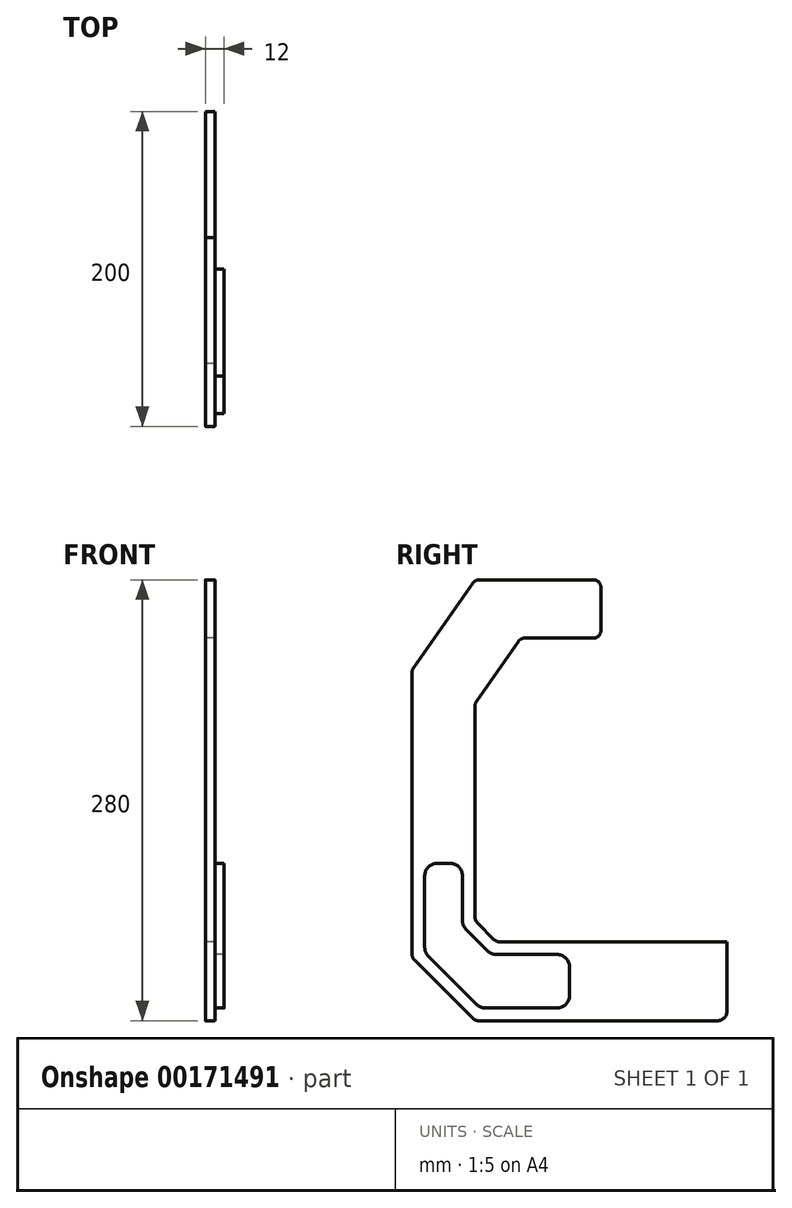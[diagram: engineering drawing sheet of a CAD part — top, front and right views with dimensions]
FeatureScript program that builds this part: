
annotation { "Feature Type Name" : "Feature", "Feature Type Description" : "" }
export const myFeature = defineFeature(function(context is Context, id is Id, definition is map)
    precondition{}
    {
        {
            var Q0;
            Q0=qCreatedBy(makeId("Right.planeOp"),FACE);
            var sketch = newSketch(context, id + "F0", { "sketchPlane" : qUnion([Q0])});
            skLineSegment(sketch, "E0", {"start": v(0, 0) * mm, "end": v(-160, 0) * mm});
            skLineSegment(sketch, "E1", {"start": v(-160, 0) * mm, "end": v(-200, 40) * mm});
            skLineSegment(sketch, "E2", {"start": v(-200, 40) * mm, "end": v(-200, 222.87) * mm});
            skLineSegment(sketch, "E3", {"start": v(-200, 222.87) * mm, "end": v(-160, 280) * mm});
            skLineSegment(sketch, "E4", {"start": v(-160, 280) * mm, "end": v(-80, 280) * mm});
            skLineSegment(sketch, "E5", {"start": v(-80, 280) * mm, "end": v(-80, 243) * mm});
            skLineSegment(sketch, "E6", {"start": v(-80, 243) * mm, "end": v(-130.97, 243) * mm});
            skLineSegment(sketch, "E7", {"start": v(-130.97, 243) * mm, "end": v(-160, 201.54) * mm});
            skLineSegment(sketch, "E8", {"start": v(-160, 201.54) * mm, "end": v(-160, 63.64) * mm});
            skLineSegment(sketch, "E9", {"start": v(-160, 63.64) * mm, "end": v(-146.36, 50) * mm});
            skLineSegment(sketch, "E10", {"start": v(-146.36, 50) * mm, "end": v(0, 50) * mm});
            skLineSegment(sketch, "E11", {"start": v(0, 50) * mm, "end": v(0, 0) * mm});
            skSolve(sketch);
        }
        {
            var Q0;
            Q0=makeQuery(id+"F0.imprint","IMPRINT",FACE,{"disambiguationData":[TD([[makeQuery(id+"F0.imprint","IMPRINT",EDGE,{"derivedFrom":sQuery(id+"F0.wireOp",EDGE,"E0")}),-1.0]])]});
            extrude(context, id + "F1", {"entities" : qUnion([Q0]), "depth" : 6 * mm});
        }
        {
            var Q0;
            Q0=makeQuery(id+"F1.opExtrude","SWEPT_EDGE",EDGE,{"disambiguationData":[OSD([sQuery(id+"F0.wireOp",EDGE,"E0"),sQuery(id+"F0.wireOp",EDGE,"E11")])]});
            fillet(context, id + "F2", {"entities" : qUnion([Q0]), "radius" : 6 * mm, "tangentPropagation" : true, "allowEdgeOverflow" : false});
        }
        {
            var Q0;
            Q0=makeQuery(id+"F1.opExtrude","SWEPT_EDGE",EDGE,{"disambiguationData":[OSD([sQuery(id+"F0.wireOp",EDGE,"E9"),sQuery(id+"F0.wireOp",EDGE,"E10")])]});
            var Q1;
            Q1=makeQuery(id+"F1.opExtrude","SWEPT_EDGE",EDGE,{"disambiguationData":[OSD([sQuery(id+"F0.wireOp",EDGE,"E8"),sQuery(id+"F0.wireOp",EDGE,"E9")])]});
            var Q2;
            Q2=makeQuery(id+"F1.opExtrude","SWEPT_EDGE",EDGE,{"disambiguationData":[OSD([sQuery(id+"F0.wireOp",EDGE,"E6"),sQuery(id+"F0.wireOp",EDGE,"E7")])]});
            var Q3;
            Q3=makeQuery(id+"F1.opExtrude","SWEPT_EDGE",EDGE,{"disambiguationData":[OSD([sQuery(id+"F0.wireOp",EDGE,"E7"),sQuery(id+"F0.wireOp",EDGE,"E8")])]});
            var Q4;
            Q4=makeQuery(id+"F1.opExtrude","SWEPT_EDGE",EDGE,{"disambiguationData":[OSD([sQuery(id+"F0.wireOp",EDGE,"E3"),sQuery(id+"F0.wireOp",EDGE,"E4")])]});
            var Q5;
            Q5=makeQuery(id+"F1.opExtrude","SWEPT_EDGE",EDGE,{"disambiguationData":[OSD([sQuery(id+"F0.wireOp",EDGE,"E2"),sQuery(id+"F0.wireOp",EDGE,"E3")])]});
            var Q6;
            Q6=makeQuery(id+"F1.opExtrude","SWEPT_EDGE",EDGE,{"disambiguationData":[OSD([sQuery(id+"F0.wireOp",EDGE,"E0"),sQuery(id+"F0.wireOp",EDGE,"E1")])]});
            var Q7;
            Q7=makeQuery(id+"F1.opExtrude","SWEPT_EDGE",EDGE,{"disambiguationData":[OSD([sQuery(id+"F0.wireOp",EDGE,"E1"),sQuery(id+"F0.wireOp",EDGE,"E2")])]});
            var Q8;
            Q8=makeQuery(id+"F1.opExtrude","SWEPT_EDGE",EDGE,{"disambiguationData":[OSD([sQuery(id+"F0.wireOp",EDGE,"E4"),sQuery(id+"F0.wireOp",EDGE,"E5")])]});
            var Q9;
            Q9=makeQuery(id+"F1.opExtrude","SWEPT_EDGE",EDGE,{"disambiguationData":[OSD([sQuery(id+"F0.wireOp",EDGE,"E5"),sQuery(id+"F0.wireOp",EDGE,"E6")])]});
            fillet(context, id + "F3", {"entities" : qUnion([Q0, Q1, Q2, Q3, Q4, Q5, Q6, Q7, Q8, Q9]), "radius" : 5 * mm, "tangentPropagation" : true, "allowEdgeOverflow" : false});
        }
        {
            var Q0;
            Q0=makeQuery(id+"F1.opExtrude","CAP_FACE",FACE,{"disambiguationData":[OSD([sQuery(id+"F0.wireOp",EDGE,"E0"),sQuery(id+"F0.wireOp",EDGE,"E1"),sQuery(id+"F0.wireOp",EDGE,"E2"),sQuery(id+"F0.wireOp",EDGE,"E3"),sQuery(id+"F0.wireOp",EDGE,"E4"),sQuery(id+"F0.wireOp",EDGE,"E5"),sQuery(id+"F0.wireOp",EDGE,"E6"),sQuery(id+"F0.wireOp",EDGE,"E7"),sQuery(id+"F0.wireOp",EDGE,"E8"),sQuery(id+"F0.wireOp",EDGE,"E9"),sQuery(id+"F0.wireOp",EDGE,"E10"),sQuery(id+"F0.wireOp",EDGE,"E11")])],"isStart":false});
            var sketch = newSketch(context, id + "F4", { "sketchPlane" : qUnion([Q0])});
            skLineSegment(sketch, "E12", {"start": v(-100, 42) * mm, "end": v(-149.67, 42) * mm});
            skLineSegment(sketch, "E13", {"start": v(-149.67, 42) * mm, "end": v(-168, 60.33) * mm});
            skLineSegment(sketch, "E14", {"start": v(-168, 60.33) * mm, "end": v(-168, 100) * mm});
            skLineSegment(sketch, "E15", {"start": v(-168, 100) * mm, "end": v(-192, 100) * mm});
            skLineSegment(sketch, "E16", {"start": v(-192, 100) * mm, "end": v(-192, 43.31) * mm});
            skLineSegment(sketch, "E17", {"start": v(-192, 43.31) * mm, "end": v(-156.69, 8) * mm});
            skLineSegment(sketch, "E18", {"start": v(-156.69, 8) * mm, "end": v(-100, 8) * mm});
            skLineSegment(sketch, "E19", {"start": v(-100, 8) * mm, "end": v(-100, 42) * mm});
            skSolve(sketch);
        }
        {
            var Q0;
            Q0=makeQuery(id+"F4.imprint","IMPRINT",FACE,{"disambiguationData":[TD([[makeQuery(id+"F4.imprint","IMPRINT",EDGE,{"derivedFrom":sQuery(id+"F4.wireOp",EDGE,"E12")}),1.0]])]});
            extrude(context, id + "F5", {"entities" : qUnion([Q0]), "depth" : 6 * mm});
        }
        {
            var Q0;
            Q0=makeQuery(id+"F5.opExtrude","SWEPT_EDGE",EDGE,{"disambiguationData":[OSD([sQuery(id+"F4.wireOp",EDGE,"E14"),sQuery(id+"F4.wireOp",EDGE,"E15")])]});
            var Q1;
            Q1=makeQuery(id+"F5.opExtrude","SWEPT_EDGE",EDGE,{"disambiguationData":[OSD([sQuery(id+"F4.wireOp",EDGE,"E15"),sQuery(id+"F4.wireOp",EDGE,"E16")])]});
            var Q2;
            Q2=makeQuery(id+"F5.opExtrude","SWEPT_EDGE",EDGE,{"disambiguationData":[OSD([sQuery(id+"F4.wireOp",EDGE,"E13"),sQuery(id+"F4.wireOp",EDGE,"E14")])]});
            var Q3;
            Q3=makeQuery(id+"F5.opExtrude","SWEPT_EDGE",EDGE,{"disambiguationData":[OSD([sQuery(id+"F4.wireOp",EDGE,"E12"),sQuery(id+"F4.wireOp",EDGE,"E13")])]});
            var Q4;
            Q4=makeQuery(id+"F5.opExtrude","SWEPT_EDGE",EDGE,{"disambiguationData":[OSD([sQuery(id+"F4.wireOp",EDGE,"E12"),sQuery(id+"F4.wireOp",EDGE,"E19")])]});
            var Q5;
            Q5=makeQuery(id+"F5.opExtrude","SWEPT_EDGE",EDGE,{"disambiguationData":[OSD([sQuery(id+"F4.wireOp",EDGE,"E18"),sQuery(id+"F4.wireOp",EDGE,"E19")])]});
            var Q6;
            Q6=makeQuery(id+"F5.opExtrude","SWEPT_EDGE",EDGE,{"disambiguationData":[OSD([sQuery(id+"F4.wireOp",EDGE,"E17"),sQuery(id+"F4.wireOp",EDGE,"E18")])]});
            var Q7;
            Q7=makeQuery(id+"F5.opExtrude","SWEPT_EDGE",EDGE,{"disambiguationData":[OSD([sQuery(id+"F4.wireOp",EDGE,"E16"),sQuery(id+"F4.wireOp",EDGE,"E17")])]});
            fillet(context, id + "F6", {"entities" : qUnion([Q0, Q1, Q2, Q3, Q4, Q5, Q6, Q7]), "radius" : 8 * mm, "tangentPropagation" : true, "allowEdgeOverflow" : false});
        }
    });
